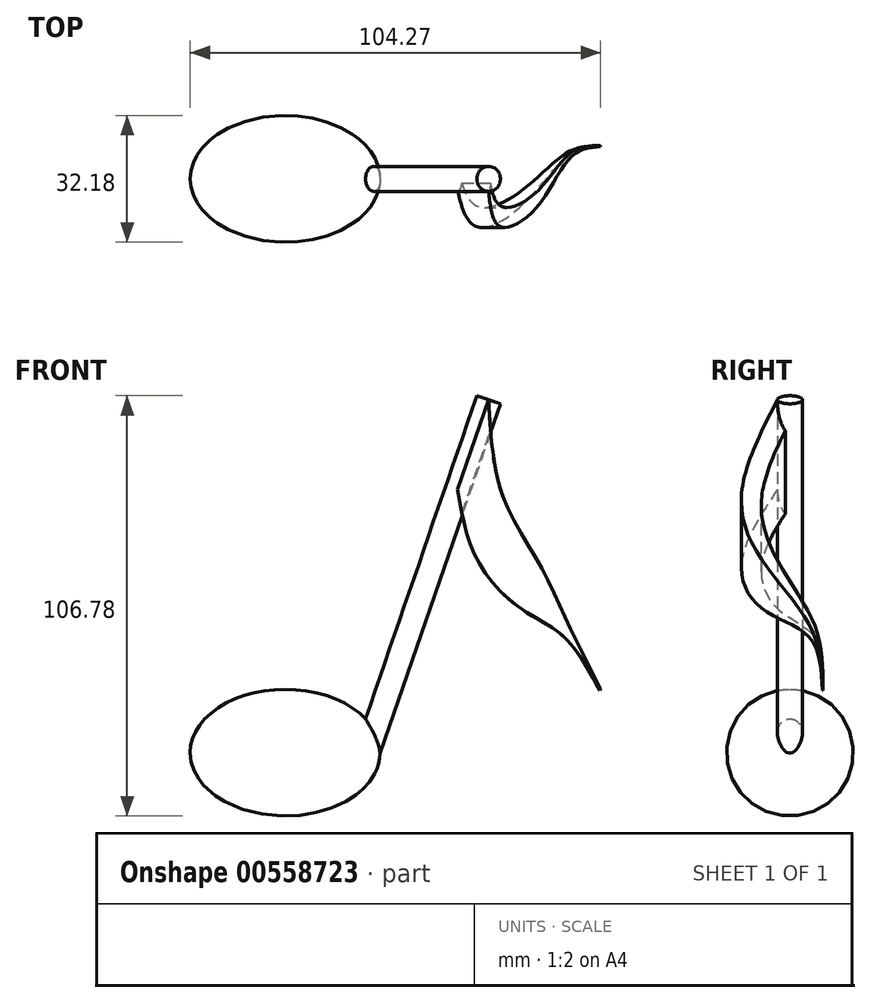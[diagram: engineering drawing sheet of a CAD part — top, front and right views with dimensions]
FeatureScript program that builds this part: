
annotation { "Feature Type Name" : "Feature", "Feature Type Description" : "" }
export const myFeature = defineFeature(function(context is Context, id is Id, definition is map)
    precondition{}
    {
        {
            var Q0;
            Q0=qCreatedBy(makeId("Front.planeOp"),FACE);
            var sketch = newSketch(context, id + "F0", { "sketchPlane" : qUnion([Q0])});
            skEllipticalArc(sketch, "E0", {});
            skLineSegment(sketch, "E1", {"start": v(-48.26, 0) * mm, "end": v(48.26, 0) * mm});
            const initialGuessF0  = {"E0": [0, 0, -1, 0, 0.04826, 0.03217333333333333, 3.141592653589793, 0]};
            skSetInitialGuess(sketch, initialGuessF0);
            skSolve(sketch);
        }
        {
            var Q0;
            Q0=makeQuery(id+"F0.imprint","IMPRINT",FACE,{"disambiguationData":[TD([[makeQuery(id+"F0.imprint","IMPRINT",EDGE,{"derivedFrom":sQuery(id+"F0.wireOp",EDGE,"E0")}),1.0]])]});
            var Q1;
            Q1=sQuery(id+"F0.wireOp",EDGE,"E0");
            var Q2;
            Q2=sQuery(id+"F0.wireOp",EDGE,"E1");
            revolve(context, id + "F1", {"entities" : qUnion([Q0]), "surfaceEntities" : qUnion([Q1]), "axis" : qUnion([Q2]), "revolveType" : RevolveType.FULL});
        }
        {
            var Q0;
            Q0=qCreatedBy(makeId("Right.planeOp"),FACE);
            var sketch = newSketch(context, id + "F2", { "sketchPlane" : qUnion([Q0])});
            skLineSegment(sketch, "E2", {"start": v(-21.06, 0) * mm, "end": v(21.06, 0) * mm, "construction": true});
            skSolve(sketch);
        }
        {
            var Q0;
            Q0=qCreatedBy(makeId("Top.planeOp"),FACE);
            var Q1;
            Q1=sQuery(id+"F2.wireOp",EDGE,"E2");
            cPlane(context, id + "F3", {"entities" : qUnion([Q0, Q1]), "cplaneType" : CPlaneType.LINE_ANGLE, "offset" : 25.4 * mm, "angle" : 19 * degree, "width" : 152.4 * mm, "height" : 152.4 * mm});
        }
        {
            var Q0;
            Q0=qCreatedBy(id+"F3.planeOp",FACE);
            var sketch = newSketch(context, id + "F4", { "sketchPlane" : qUnion([Q0])});
            skCircle(sketch, "E3", {"center": v(39.37, 0) * mm, "radius": 6.35 * mm});
            skSolve(sketch);
        }
        {
            var Q0;
            Q0=qSketchRegion(id+"F4",true);
            extrude(context, id + "F5", {"entities" : qUnion([Q0]), "operationType" : NewBodyOperationType.ADD, "oppositeDirection" : true, "depth" : 203.2 * mm, "hasSecondDirection" : true, "secondDirectionOppositeDirection" : true, "secondDirectionDepth" : 2.54 * mm});
        }
        {
            var Q0;
            Q0=qCreatedBy(id+"F3.planeOp",FACE);
            var Q1;
            Q1=sQuery(id+"F2.wireOp",EDGE,"E2");
            cPlane(context, id + "F6", {"entities" : qUnion([Q0, Q1]), "cplaneType" : CPlaneType.LINE_ANGLE, "offset" : 25.4 * mm, "angle" : 90 * degree, "width" : 152.4 * mm, "height" : 152.4 * mm});
        }
        {
            var Q0;
            Q0=qCreatedBy(id+"F6.planeOp",FACE);
            cPlane(context, id + "F7", {"entities" : qUnion([Q0]), "cplaneType" : CPlaneType.OFFSET, "offset" : 39.37 * mm, "width" : 152.4 * mm, "height" : 152.4 * mm});
        }
        {
            var Q0;
            Q0=qCreatedBy(id+"F7.planeOp",FACE);
            var sketch = newSketch(context, id + "F8", { "sketchPlane" : qUnion([Q0])});
            skLineSegment(sketch, "E4.bottom", {"start": v(-6.35, 203.2) * mm, "end": v(6.35, 203.2) * mm});
            skLineSegment(sketch, "E4.top", {"start": v(-6.35, 154.94) * mm, "end": v(6.35, 154.94) * mm});
            skLineSegment(sketch, "E4.left", {"start": v(-6.35, 203.2) * mm, "end": v(-6.35, 154.94) * mm});
            skLineSegment(sketch, "E4.right", {"start": v(6.35, 203.2) * mm, "end": v(6.35, 154.94) * mm});
            skPoint(sketch, "E4.middle", {"position": v(0, 179.07) * mm});
            skSolve(sketch);
        }
        {
            var Q0;
            Q0=qCreatedBy(id+"F7.planeOp",FACE);
            cPlane(context, id + "F9", {"entities" : qUnion([Q0]), "cplaneType" : CPlaneType.OFFSET, "offset" : 25.4 * mm, "width" : 152.4 * mm, "height" : 152.4 * mm});
        }
        {
            var Q0;
            Q0=qCreatedBy(id+"F9.planeOp",FACE);
            var sketch = newSketch(context, id + "F10", { "sketchPlane" : qUnion([Q0])});
            skLineSegment(sketch, "E5.bottom", {"start": v(-14.54, 156.18) * mm, "end": v(-24.7, 156.18) * mm});
            skLineSegment(sketch, "E5.top", {"start": v(-14.54, 120.62) * mm, "end": v(-24.7, 120.62) * mm});
            skLineSegment(sketch, "E5.left", {"start": v(-14.54, 156.18) * mm, "end": v(-14.54, 120.62) * mm});
            skLineSegment(sketch, "E5.right", {"start": v(-24.7, 156.18) * mm, "end": v(-24.7, 120.62) * mm});
            skPoint(sketch, "E5.middle", {"position": v(-19.62, 138.4) * mm});
            skSolve(sketch);
        }
        {
            var Q0;
            Q0=qCreatedBy(id+"F9.planeOp",FACE);
            cPlane(context, id + "F11", {"entities" : qUnion([Q0]), "cplaneType" : CPlaneType.OFFSET, "offset" : 25.4 * mm, "width" : 152.4 * mm, "height" : 152.4 * mm});
        }
        {
            var Q0;
            Q0=qCreatedBy(id+"F11.planeOp",FACE);
            var sketch = newSketch(context, id + "F12", { "sketchPlane" : qUnion([Q0])});
            skLineSegment(sketch, "E6.bottom", {"start": v(-13.4, 107.98) * mm, "end": v(-5.77, 107.98) * mm});
            skLineSegment(sketch, "E6.top", {"start": v(-13.4, 133.38) * mm, "end": v(-5.77, 133.38) * mm});
            skLineSegment(sketch, "E6.left", {"start": v(-13.4, 107.98) * mm, "end": v(-13.4, 133.38) * mm});
            skLineSegment(sketch, "E6.right", {"start": v(-5.77, 107.98) * mm, "end": v(-5.77, 133.38) * mm});
            skPoint(sketch, "E6.middle", {"position": v(-9.58, 120.68) * mm});
            skSolve(sketch);
        }
        {
            var Q0;
            Q0=qCreatedBy(id+"F11.planeOp",FACE);
            cPlane(context, id + "F13", {"entities" : qUnion([Q0]), "cplaneType" : CPlaneType.OFFSET, "offset" : 25.4 * mm, "width" : 152.4 * mm, "height" : 152.4 * mm});
        }
        {
            var Q0;
            Q0=qCreatedBy(id+"F13.planeOp",FACE);
            var sketch = newSketch(context, id + "F14", { "sketchPlane" : qUnion([Q0])});
            skLineSegment(sketch, "E7.bottom", {"start": v(12.7, 107.78) * mm, "end": v(10.16, 107.78) * mm});
            skLineSegment(sketch, "E7.top", {"start": v(12.7, 101.43) * mm, "end": v(10.16, 101.43) * mm});
            skLineSegment(sketch, "E7.left", {"start": v(12.7, 107.78) * mm, "end": v(12.7, 101.43) * mm});
            skLineSegment(sketch, "E7.right", {"start": v(10.16, 107.78) * mm, "end": v(10.16, 101.43) * mm});
            skPoint(sketch, "E7.middle", {"position": v(11.43, 104.6) * mm});
            skSolve(sketch);
        }
        {
            var Q0;
            Q0=qCreatedBy(id+"F13.planeOp",FACE);
            cPlane(context, id + "F15", {"entities" : qUnion([Q0]), "cplaneType" : CPlaneType.OFFSET, "offset" : 25.4 * mm, "width" : 152.4 * mm, "height" : 152.4 * mm});
        }
        {
            var Q0;
            Q0=qCreatedBy(id+"F15.planeOp",FACE);
            var sketch = newSketch(context, id + "F16", { "sketchPlane" : qUnion([Q0])});
            skLineSegment(sketch, "E8.bottom", {"start": v(16.41, 82.88) * mm, "end": v(16.9, 82.88) * mm});
            skLineSegment(sketch, "E8.top", {"start": v(16.41, 81.91) * mm, "end": v(16.9, 81.91) * mm});
            skLineSegment(sketch, "E8.left", {"start": v(16.41, 82.88) * mm, "end": v(16.41, 81.91) * mm});
            skLineSegment(sketch, "E8.right", {"start": v(16.9, 82.88) * mm, "end": v(16.9, 81.91) * mm});
            skPoint(sketch, "E8.middle", {"position": v(16.66, 82.4) * mm});
            skSolve(sketch);
        }
        {
            var Q1;
            Q1=qSketchRegion(id+"F8",true);
            var Q2;
            Q2=qSketchRegion(id+"F10",true);
            var Q3;
            Q3=qSketchRegion(id+"F12",true);
            var Q4;
            Q4=qSketchRegion(id+"F14",true);
            var Q5;
            Q5=qSketchRegion(id+"F16",true);
            loft(context, id + "F17", {"operationType" : NewBodyOperationType.ADD, "sheetProfilesArray" : [{ "sheetProfileEntities" : qUnion([Q1]) }, { "sheetProfileEntities" : qUnion([Q2]) }, { "sheetProfileEntities" : qUnion([Q3]) }, { "sheetProfileEntities" : qUnion([Q4]) }, { "sheetProfileEntities" : qUnion([Q5]) }]});
        }
        {
            var Q0;
            Q0=makeQuery(id+"F1.opRevolve","SWEPT_BODY",BODY,{"disambiguationData":[OSD([sQuery(id+"F0.wireOp",EDGE,"E0"),sQuery(id+"F0.wireOp",EDGE,"E1")])]});
            var Q1;
            Q1=qCreatedBy(makeId("Origin.pointOp"),VERTEX);
            transform(context, id + "F18", {"entities" : qUnion([Q0]), "transformType" : TransformType.SCALE_UNIFORMLY, "scale" : 0.5, "scalePoint" : qUnion([Q1]), "makeCopy" : false});
        }
    });
